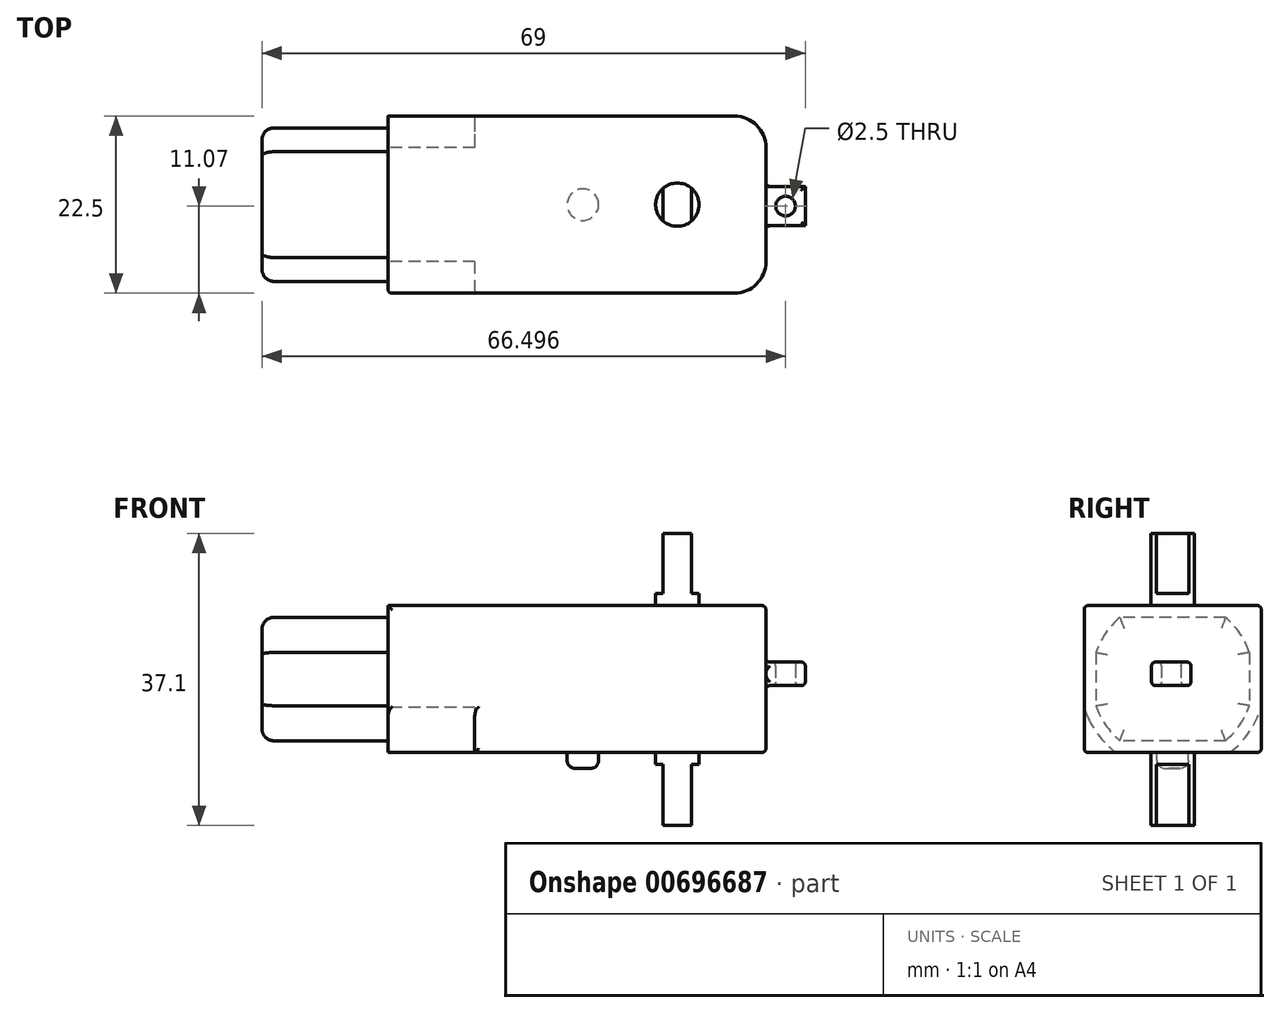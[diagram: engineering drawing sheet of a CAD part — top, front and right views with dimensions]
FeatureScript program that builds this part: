
annotation { "Feature Type Name" : "Feature", "Feature Type Description" : "" }
export const myFeature = defineFeature(function(context is Context, id is Id, definition is map)
    precondition{}
    {
        {
            var Q0;
            Q0=qCreatedBy(makeId("Top.planeOp"),FACE);
            var sketch = newSketch(context, id + "F0", { "sketchPlane" : qUnion([Q0])});
            skLineSegment(sketch, "E0.bottom", {"start": v(-14.02, 13.93) * mm, "end": v(33.98, 13.93) * mm});
            skLineSegment(sketch, "E0.top", {"start": v(-14.02, -8.57) * mm, "end": v(33.98, -8.57) * mm});
            skLineSegment(sketch, "E0.left", {"start": v(-14.02, 13.93) * mm, "end": v(-14.02, -8.57) * mm});
            skLineSegment(sketch, "E0.right", {"start": v(33.98, 13.93) * mm, "end": v(33.98, -8.57) * mm});
            skLineSegment(sketch, "E1", {"start": v(33.98, -8.57) * mm, "end": v(11.48, 13.93) * mm, "construction": true});
            skPoint(sketch, "E2", {"position": v(22.73, 2.68) * mm});
            skCircle(sketch, "E3", {"center": v(22.73, 2.68) * mm, "radius": 2.75 * mm});
            skCircle(sketch, "E4", {"center": v(10.73, 2.68) * mm, "radius": 2 * mm});
            skLineSegment(sketch, "E5.bottom", {"start": v(20.93, 5.43) * mm, "end": v(24.53, 5.43) * mm});
            skLineSegment(sketch, "E5.top", {"start": v(20.93, -0.07) * mm, "end": v(24.53, -0.07) * mm});
            skLineSegment(sketch, "E5.left", {"start": v(20.93, 5.43) * mm, "end": v(20.93, -0.07) * mm});
            skLineSegment(sketch, "E5.right", {"start": v(24.53, 5.43) * mm, "end": v(24.53, -0.07) * mm});
            skPoint(sketch, "E6", {"position": v(22.73, 5.43) * mm});
            skSolve(sketch);
        }
        {
            var Q0;
            Q0=makeQuery(id+"F0.imprint","IMPRINT",FACE,{"disambiguationData":[TD([[makeQuery(id+"F0.imprint","IMPRINT",EDGE,{"derivedFrom":sQuery(id+"F0.wireOp",EDGE,"E0.bottom")}),-1.0]])]});
            var Q1;
            {var subQ0=sQuery(id+"F0.wireOp",EDGE,"txEnJRYb-Wpty-XLPx-xXNW-ixA6nXr7amaz");Q1=makeQuery(id+"F0.imprint","IMPRINT",FACE,{"disambiguationData":[TD([[makeQuery(id+"F0.imprint","IMPRINT",EDGE,{"derivedFrom":subQ0}),-1.0]])]});}
            var Q2;
            {var subQ5=sQuery(id+"F0.wireOp",EDGE,"nBWcCEPt-qENP-5VbL-EOs8-Mcf2W3Knmk6I");Q2=makeQuery(id+"F0.imprint","IMPRINT",FACE,{"disambiguationData":[TD([[makeQuery(id+"F0.imprint","IMPRINT",EDGE,{"derivedFrom":subQ5}),-1.0]])]});}
            var Q3;
            {var subQ0=sQuery(id+"F0.wireOp",EDGE,"E0.right");Q3=makeQuery(id+"F0.imprint","IMPRINT",FACE,{"disambiguationData":[TD([[makeQuery(id+"F0.imprint","IMPRINT",EDGE,{"derivedFrom":subQ0}),-1.0]])]});}
            var Q4;
            {var subQ2=sQuery(id+"F0.wireOp",EDGE,"txEnJRYb-Wpty-XLPx-xXNW-ixA6nXr7amaz");Q4=makeQuery(id+"F0.imprint","IMPRINT",FACE,{"disambiguationData":[TD([[makeQuery(id+"F0.imprint","IMPRINT",EDGE,{"derivedFrom":subQ2}),1.0]])]});}
            var Q5;
            Q5=makeQuery(id+"F0.imprint","IMPRINT",FACE,{"disambiguationData":[TD([[makeQuery(id+"F0.imprint","IMPRINT",EDGE,{"derivedFrom":sQuery(id+"F0.wireOp",EDGE,"E3")}),1.0]])]});
            var Q6;
            Q6=makeQuery(id+"F0.imprint","IMPRINT",FACE,{"disambiguationData":[TD([[makeQuery(id+"F0.imprint","IMPRINT",EDGE,{"derivedFrom":sQuery(id+"F0.wireOp",EDGE,"E4")}),1.0]])]});
            var Q7;
            {var subQ0=sQuery(id+"F0.wireOp",EDGE,"E5.right");var subQ1=sQuery(id+"F0.wireOp",EDGE,"E3");var subQ2=makeQuery(id+"F0.imprint","INTERSECT",VERTEX,{"disambiguationData":[OD(0.0)],"derivedFrom":[subQ1,subQ0]});Q7=makeQuery(id+"F0.imprint","IMPRINT",FACE,{"disambiguationData":[TD([[makeQuery(id+"F0.imprint","IMPRINT",EDGE,{"disambiguationData":[TD([[subQ2,1.0]])],"derivedFrom":subQ1}),1.0]])]});}
            var Q8;
            {var subQ0=sQuery(id+"F0.wireOp",EDGE,"E5.left");var subQ1=sQuery(id+"F0.wireOp",EDGE,"E3");var subQ2=makeQuery(id+"F0.imprint","INTERSECT",VERTEX,{"disambiguationData":[OD(0.0)],"derivedFrom":[subQ1,subQ0]});Q8=makeQuery(id+"F0.imprint","IMPRINT",FACE,{"disambiguationData":[TD([[makeQuery(id+"F0.imprint","IMPRINT",EDGE,{"disambiguationData":[TD([[subQ2,-1.0]])],"derivedFrom":subQ1}),1.0]])]});}
            var Q9;
            {var subQ0=sQuery(id+"F0.wireOp",EDGE,"E5.left");var subQ1=sQuery(id+"F0.wireOp",EDGE,"E3");var subQ2=makeQuery(id+"F0.imprint","INTERSECT",VERTEX,{"disambiguationData":[OD(1.0)],"derivedFrom":[subQ1,subQ0]});Q9=makeQuery(id+"F0.imprint","IMPRINT",FACE,{"disambiguationData":[TD([[makeQuery(id+"F0.imprint","IMPRINT",EDGE,{"disambiguationData":[TD([[subQ2,-1.0]])],"derivedFrom":subQ1}),-1.0]])]});}
            var Q10;
            {var subQ0=sQuery(id+"F0.wireOp",EDGE,"E5.top");var subQ1=sQuery(id+"F0.wireOp",EDGE,"E3");var subQ2=makeQuery(id+"F0.imprint","INTERSECT",VERTEX,{"derivedFrom":[subQ1,subQ0]});Q10=makeQuery(id+"F0.imprint","IMPRINT",FACE,{"disambiguationData":[TD([[makeQuery(id+"F0.imprint","IMPRINT",EDGE,{"disambiguationData":[TD([[subQ2,-1.0]])],"derivedFrom":subQ1}),-1.0]])]});}
            var Q11;
            {var subQ0=sQuery(id+"F0.wireOp",EDGE,"E5.bottom");var subQ1=sQuery(id+"F0.wireOp",EDGE,"E3");var subQ2=makeQuery(id+"F0.imprint","INTERSECT",VERTEX,{"derivedFrom":[subQ1,subQ0]});Q11=makeQuery(id+"F0.imprint","IMPRINT",FACE,{"disambiguationData":[TD([[makeQuery(id+"F0.imprint","IMPRINT",EDGE,{"disambiguationData":[TD([[subQ2,1.0]])],"derivedFrom":subQ1}),-1.0]])]});}
            var Q12;
            {var subQ0=sQuery(id+"F0.wireOp",EDGE,"E5.bottom");var subQ1=sQuery(id+"F0.wireOp",EDGE,"E3");var subQ2=makeQuery(id+"F0.imprint","INTERSECT",VERTEX,{"derivedFrom":[subQ1,subQ0]});Q12=makeQuery(id+"F0.imprint","IMPRINT",FACE,{"disambiguationData":[TD([[makeQuery(id+"F0.imprint","IMPRINT",EDGE,{"disambiguationData":[TD([[subQ2,-1.0]])],"derivedFrom":subQ1}),-1.0]])]});}
            extrude(context, id + "F1", {"entities" : qUnion([Q0, Q1, Q2, Q3, Q4, Q5, Q6, Q7, Q8, Q9, Q10, Q11, Q12]), "depth" : 18.67 * mm, "offsetDistance" : 25 * mm});
        }
        {
            var Q0;
            Q0=makeQuery(id+"F1.opExtrude","SWEPT_EDGE",EDGE,{"disambiguationData":[OSD([sQuery(id+"F0.wireOp",EDGE,"E0.bottom"),sQuery(id+"F0.wireOp",EDGE,"E0.right")])]});
            var Q1;
            Q1=makeQuery(id+"F1.opExtrude","SWEPT_EDGE",EDGE,{"disambiguationData":[OSD([sQuery(id+"F0.wireOp",EDGE,"E0.top"),sQuery(id+"F0.wireOp",EDGE,"E0.right")])]});
            fillet(context, id + "F2", {"entities" : qUnion([Q0, Q1]), "radius" : 4 * mm, "tangentPropagation" : true, "allowEdgeOverflow" : false});
        }
        {
            var Q0;
            Q0=makeQuery(id+"F1.opExtrude","SWEPT_FACE",FACE,{"disambiguationData":[OSD([sQuery(id+"F0.wireOp",EDGE,"E0.left")])]});
            var sketch = newSketch(context, id + "F3", { "sketchPlane" : qUnion([Q0])});
            skLineSegment(sketch, "E7", {"start": v(4.57, 18.67) * mm, "end": v(4.57, 0) * mm, "construction": true});
            skLineSegment(sketch, "E8", {"start": v(-9.93, 18.67) * mm, "end": v(-9.93, 0) * mm, "construction": true});
            skCircle(sketch, "E9", {"center": v(-2.68, 9.33) * mm, "radius": 11.82 * mm});
            skSolve(sketch);
        }
        {
            var Q0;
            {var subQ0=sQuery(id+"F3.wireOp",EDGE,"E9");var subQ1=sQuery(id+"F0.wireOp",EDGE,"E0.left");var subQ2=makeQuery(id+"F1.opExtrude","CAP_EDGE",EDGE,{"disambiguationData":[OSD([subQ1])],"isStart":false});var subQ3=makeQuery(id+"F3.imprint","INTERSECT",VERTEX,{"disambiguationData":[OD(0.0)],"derivedFrom":[subQ2,subQ0]});Q0=makeQuery(id+"F3.imprint","IMPRINT",FACE,{"disambiguationData":[TD([[makeQuery(id+"F3.imprint","IMPRINT",EDGE,{"disambiguationData":[TD([[subQ3,1.0]])],"derivedFrom":subQ0}),-1.0]])]});}
            var Q1;
            {var subQ0=sQuery(id+"F3.wireOp",EDGE,"E9");var subQ1=sQuery(id+"F0.wireOp",EDGE,"E0.left");var subQ2=makeQuery(id+"F1.opExtrude","CAP_EDGE",EDGE,{"disambiguationData":[OSD([subQ1])],"isStart":false});var subQ3=makeQuery(id+"F3.imprint","INTERSECT",VERTEX,{"disambiguationData":[OD(1.0)],"derivedFrom":[subQ2,subQ0]});Q1=makeQuery(id+"F3.imprint","IMPRINT",FACE,{"disambiguationData":[TD([[makeQuery(id+"F3.imprint","IMPRINT",EDGE,{"disambiguationData":[TD([[subQ3,-1.0]])],"derivedFrom":subQ0}),-1.0]])]});}
            var Q2;
            {var subQ0=sQuery(id+"F3.wireOp",EDGE,"E9");var subQ1=sQuery(id+"F0.wireOp",EDGE,"E0.left");var subQ4=makeQuery(id+"F1.opExtrude","CAP_EDGE",EDGE,{"disambiguationData":[OSD([subQ1])],"isStart":true});var subQ5=makeQuery(id+"F3.imprint","INTERSECT",VERTEX,{"disambiguationData":[OD(0.0)],"derivedFrom":[subQ4,subQ0]});Q2=makeQuery(id+"F3.imprint","IMPRINT",FACE,{"disambiguationData":[TD([[makeQuery(id+"F3.imprint","IMPRINT",EDGE,{"disambiguationData":[TD([[subQ5,1.0]])],"derivedFrom":subQ0}),-1.0]])]});}
            var Q3;
            {var subQ0=sQuery(id+"F3.wireOp",EDGE,"E9");var subQ1=sQuery(id+"F0.wireOp",EDGE,"E0.left");var subQ2=makeQuery(id+"F1.opExtrude","CAP_EDGE",EDGE,{"disambiguationData":[OSD([subQ1])],"isStart":true});var subQ3=makeQuery(id+"F3.imprint","INTERSECT",VERTEX,{"disambiguationData":[OD(1.0)],"derivedFrom":[subQ2,subQ0]});Q3=makeQuery(id+"F3.imprint","IMPRINT",FACE,{"disambiguationData":[TD([[makeQuery(id+"F3.imprint","IMPRINT",EDGE,{"disambiguationData":[TD([[subQ3,-1.0]])],"derivedFrom":subQ0}),-1.0]])]});}
            extrude(context, id + "F4", {"entities" : qUnion([Q0, Q1, Q2, Q3]), "operationType" : NewBodyOperationType.REMOVE, "oppositeDirection" : true, "depth" : 11 * mm, "offsetDistance" : 25 * mm});
        }
        {
            var Q0;
            Q0=makeQuery(id+"F1.opExtrude","SWEPT_FACE",FACE,{"disambiguationData":[OSD([sQuery(id+"F0.wireOp",EDGE,"E0.left")])]});
            var sketch = newSketch(context, id + "F5", { "sketchPlane" : qUnion([Q0])});
            skLineSegment(sketch, "E10.0", {"start": v(-9.4, 17.17) * mm, "end": v(4.03, 17.17) * mm});
            skArc(sketch, "E10.1", {"start": v(7.07, 12.72) * mm, "mid": v(5.84, 15.14) * mm, "end": v(4.03, 17.17) * mm});
            skArc(sketch, "E10.2", {"start": v(-9.4, 17.17) * mm, "mid": v(-11.21, 15.14) * mm, "end": v(-12.43, 12.72) * mm});
            skLineSegment(sketch, "E10.3", {"start": v(7.07, 12.72) * mm, "end": v(7.07, 5.95) * mm});
            skLineSegment(sketch, "E10.4", {"start": v(-12.43, 12.72) * mm, "end": v(-12.43, 5.95) * mm});
            skArc(sketch, "E10.5", {"start": v(-12.43, 5.95) * mm, "mid": v(-11.21, 3.53) * mm, "end": v(-9.4, 1.5) * mm});
            skLineSegment(sketch, "E10.6", {"start": v(-9.4, 1.5) * mm, "end": v(4.03, 1.5) * mm});
            skArc(sketch, "E10.7", {"start": v(4.03, 1.5) * mm, "mid": v(5.84, 3.53) * mm, "end": v(7.07, 5.95) * mm});
            skSolve(sketch);
        }
        {
            var Q0;
            Q0=makeQuery(id+"F5.imprint","IMPRINT",FACE,{"disambiguationData":[TD([[makeQuery(id+"F5.imprint","IMPRINT",EDGE,{"derivedFrom":sQuery(id+"F5.wireOp",EDGE,"E10.0")}),-1.0]])]});
            extrude(context, id + "F6", {"entities" : qUnion([Q0]), "operationType" : NewBodyOperationType.ADD, "depth" : 16 * mm, "offsetDistance" : 25 * mm});
        }
        {
            var Q0;
            Q0=makeQuery(id+"F0.imprint","IMPRINT",FACE,{"disambiguationData":[TD([[makeQuery(id+"F0.imprint","IMPRINT",EDGE,{"derivedFrom":sQuery(id+"F0.wireOp",EDGE,"E3")}),1.0]])]});
            extrude(context, id + "F7", {"entities" : qUnion([Q0]), "operationType" : NewBodyOperationType.ADD, "oppositeDirection" : true, "depth" : 9.25 * mm, "offsetDistance" : 25 * mm, "hasSecondDirection" : true, "secondDirectionOppositeDirection" : false, "secondDirectionDepth" : 27.85 * mm});
        }
        {
            var Q0;
            Q0=makeQuery(id+"F0.imprint","IMPRINT",FACE,{"disambiguationData":[TD([[makeQuery(id+"F0.imprint","IMPRINT",EDGE,{"derivedFrom":sQuery(id+"F0.wireOp",EDGE,"E4")}),1.0]])]});
            extrude(context, id + "F8", {"entities" : qUnion([Q0]), "operationType" : NewBodyOperationType.ADD, "oppositeDirection" : true, "depth" : 2 * mm, "offsetDistance" : 25 * mm});
        }
        {
            var Q0;
            Q0=makeQuery(id+"F8.opExtrude","CAP_EDGE",EDGE,{"disambiguationData":[OSD([sQuery(id+"F0.wireOp",EDGE,"E4")])],"isStart":false});
            fillet(context, id + "F9", {"entities" : qUnion([Q0]), "radius" : 1 * mm, "tangentPropagation" : true, "allowEdgeOverflow" : false});
        }
        {
            var Q0;
            Q0=makeQuery(id+"F1.opExtrude","SWEPT_FACE",FACE,{"disambiguationData":[OSD([sQuery(id+"F0.wireOp",EDGE,"E0.right")])]});
            var sketch = newSketch(context, id + "F10", { "sketchPlane" : qUnion([Q0])});
            skLineSegment(sketch, "E11.bottom", {"start": v(0, 11.5) * mm, "end": v(5, 11.5) * mm});
            skLineSegment(sketch, "E11.top", {"start": v(0, 8.5) * mm, "end": v(5, 8.5) * mm});
            skLineSegment(sketch, "E11.left", {"start": v(0, 11.5) * mm, "end": v(0, 8.5) * mm});
            skLineSegment(sketch, "E11.right", {"start": v(5, 11.5) * mm, "end": v(5, 8.5) * mm});
            skLineSegment(sketch, "E12", {"start": v(0, 18.67) * mm, "end": v(0, 0) * mm, "construction": true});
            skSolve(sketch);
        }
        {
            var Q0;
            Q0=makeQuery(id+"F10.imprint","IMPRINT",FACE,{"disambiguationData":[TD([[makeQuery(id+"F10.imprint","IMPRINT",EDGE,{"derivedFrom":sQuery(id+"F10.wireOp",EDGE,"E11.bottom")}),-1.0]])]});
            extrude(context, id + "F11", {"entities" : qUnion([Q0]), "operationType" : NewBodyOperationType.ADD, "depth" : 5 * mm, "offsetDistance" : 25 * mm});
        }
        {
            var Q0;
            Q0=makeQuery(id+"F11.opExtrude","SWEPT_FACE",FACE,{"disambiguationData":[OSD([sQuery(id+"F10.wireOp",EDGE,"E11.top")])]});
            var sketch = newSketch(context, id + "F12", { "sketchPlane" : qUnion([Q0])});
            skLineSegment(sketch, "E13", {"start": v(33.98, 0) * mm, "end": v(38.98, -5) * mm, "construction": true});
            skCircle(sketch, "E14", {"center": v(36.48, -2.5) * mm, "radius": 1.25 * mm});
            skSolve(sketch);
        }
        {
            var Q0;
            Q0=makeQuery(id+"F12.imprint","IMPRINT",FACE,{"disambiguationData":[TD([[makeQuery(id+"F12.imprint","IMPRINT",EDGE,{"derivedFrom":sQuery(id+"F12.wireOp",EDGE,"E14")}),1.0]])]});
            extrude(context, id + "F13", {"entities" : qUnion([Q0]), "operationType" : NewBodyOperationType.REMOVE, "endBound" : BoundingType.UP_TO_NEXT, "oppositeDirection" : true, "depth" : 25 * mm, "offsetDistance" : 25 * mm});
        }
        {
            var Q0;
            Q0=makeQuery(id+"F11.opExtrude","SWEPT_FACE",FACE,{"disambiguationData":[OSD([sQuery(id+"F10.wireOp",EDGE,"E11.top")])]});
            var Q1;
            Q1=makeQuery(id+"F1.opExtrude","SWEPT_FACE",FACE,{"disambiguationData":[OSD([sQuery(id+"F0.wireOp",EDGE,"E0.top")])]});
            var Q2;
            Q2=makeQuery(id+"F11.opExtrude","SWEPT_FACE",FACE,{"disambiguationData":[OSD([sQuery(id+"F10.wireOp",EDGE,"E11.bottom")])]});
            fillet(context, id + "F14", {"entities" : qUnion([Q0, Q1, Q2]), "radius" : 0.5 * mm, "tangentPropagation" : true, "allowEdgeOverflow" : false});
        }
        {
            var Q0;
            Q0=makeQuery(id+"F6.opExtrude","CAP_FACE",FACE,{"disambiguationData":[OSD([sQuery(id+"F5.wireOp",EDGE,"E10.0"),sQuery(id+"F5.wireOp",EDGE,"E10.1"),sQuery(id+"F5.wireOp",EDGE,"E10.2"),sQuery(id+"F5.wireOp",EDGE,"E10.3"),sQuery(id+"F5.wireOp",EDGE,"E10.4"),sQuery(id+"F5.wireOp",EDGE,"E10.5"),sQuery(id+"F5.wireOp",EDGE,"E10.6"),sQuery(id+"F5.wireOp",EDGE,"E10.7")])],"isStart":false});
            fillet(context, id + "F15", {"entities" : qUnion([Q0]), "radius" : 1.5 * mm, "tangentPropagation" : true, "allowEdgeOverflow" : false});
        }
        {
            var Q0;
            {var subQ0=sQuery(id+"F0.wireOp",EDGE,"E5.left");var subQ1=sQuery(id+"F0.wireOp",EDGE,"E3");var subQ2=makeQuery(id+"F0.imprint","INTERSECT",VERTEX,{"disambiguationData":[OD(0.0)],"derivedFrom":[subQ1,subQ0]});Q0=makeQuery(id+"F0.imprint","IMPRINT",FACE,{"disambiguationData":[TD([[makeQuery(id+"F0.imprint","IMPRINT",EDGE,{"disambiguationData":[TD([[subQ2,-1.0]])],"derivedFrom":subQ1}),1.0]])]});}
            var Q1;
            {var subQ0=sQuery(id+"F0.wireOp",EDGE,"E5.right");var subQ1=sQuery(id+"F0.wireOp",EDGE,"E3");var subQ2=makeQuery(id+"F0.imprint","INTERSECT",VERTEX,{"disambiguationData":[OD(0.0)],"derivedFrom":[subQ1,subQ0]});Q1=makeQuery(id+"F0.imprint","IMPRINT",FACE,{"disambiguationData":[TD([[makeQuery(id+"F0.imprint","IMPRINT",EDGE,{"disambiguationData":[TD([[subQ2,1.0]])],"derivedFrom":subQ1}),1.0]])]});}
            extrude(context, id + "F16", {"entities" : qUnion([Q0, Q1]), "operationType" : NewBodyOperationType.ADD, "oppositeDirection" : true, "depth" : 1.5 * mm, "offsetDistance" : 25 * mm, "hasSecondDirection" : true, "secondDirectionOppositeDirection" : false, "secondDirectionDepth" : 20.2 * mm});
        }
    });
